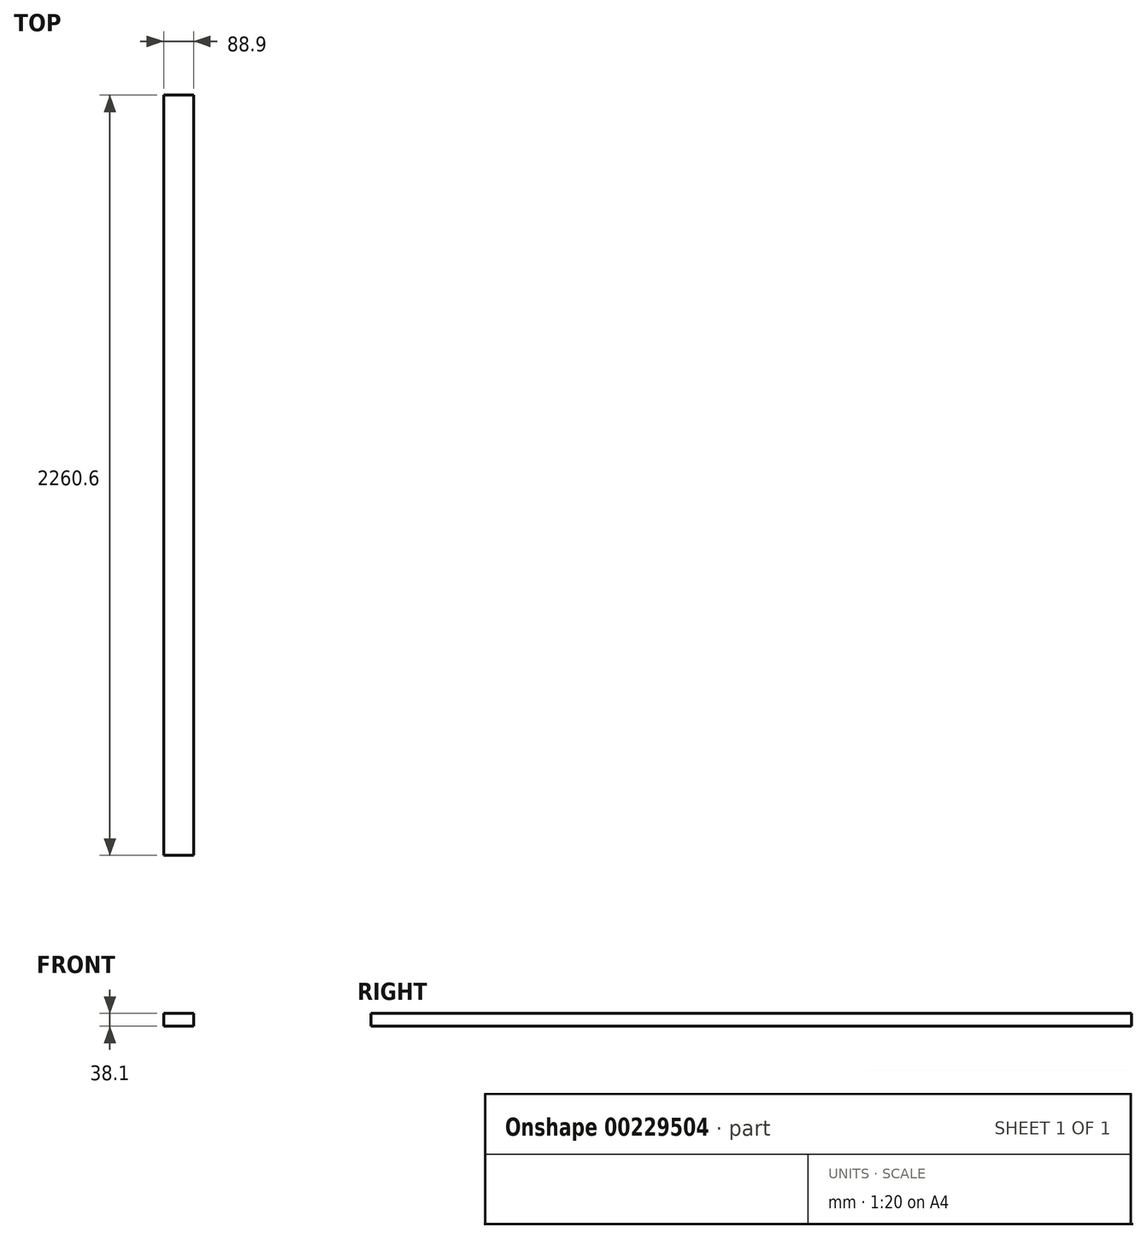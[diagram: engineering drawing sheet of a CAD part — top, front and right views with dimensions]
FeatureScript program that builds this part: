
annotation { "Feature Type Name" : "Feature", "Feature Type Description" : "" }
export const myFeature = defineFeature(function(context is Context, id is Id, definition is map)
    precondition{}
    {
        {
            var Q0;
            Q0=qCreatedBy(makeId("Front.planeOp"),FACE);
            var sketch = newSketch(context, id + "F0", { "sketchPlane" : qUnion([Q0])});
            skLineSegment(sketch, "E0.bottom", {"start": v(0, 0) * mm, "end": v(88.9, 0) * mm});
            skLineSegment(sketch, "E0.top", {"start": v(0, -38.1) * mm, "end": v(88.9, -38.1) * mm});
            skLineSegment(sketch, "E0.left", {"start": v(0, 0) * mm, "end": v(0, -38.1) * mm});
            skLineSegment(sketch, "E0.right", {"start": v(88.9, 0) * mm, "end": v(88.9, -38.1) * mm});
            skSolve(sketch);
        }
        {
            var Q0;
            Q0=qSketchRegion(id+"F0",true);
            extrude(context, id + "F1", {"entities" : qUnion([Q0]), "depth" : 2260.6 * mm});
        }
    });
